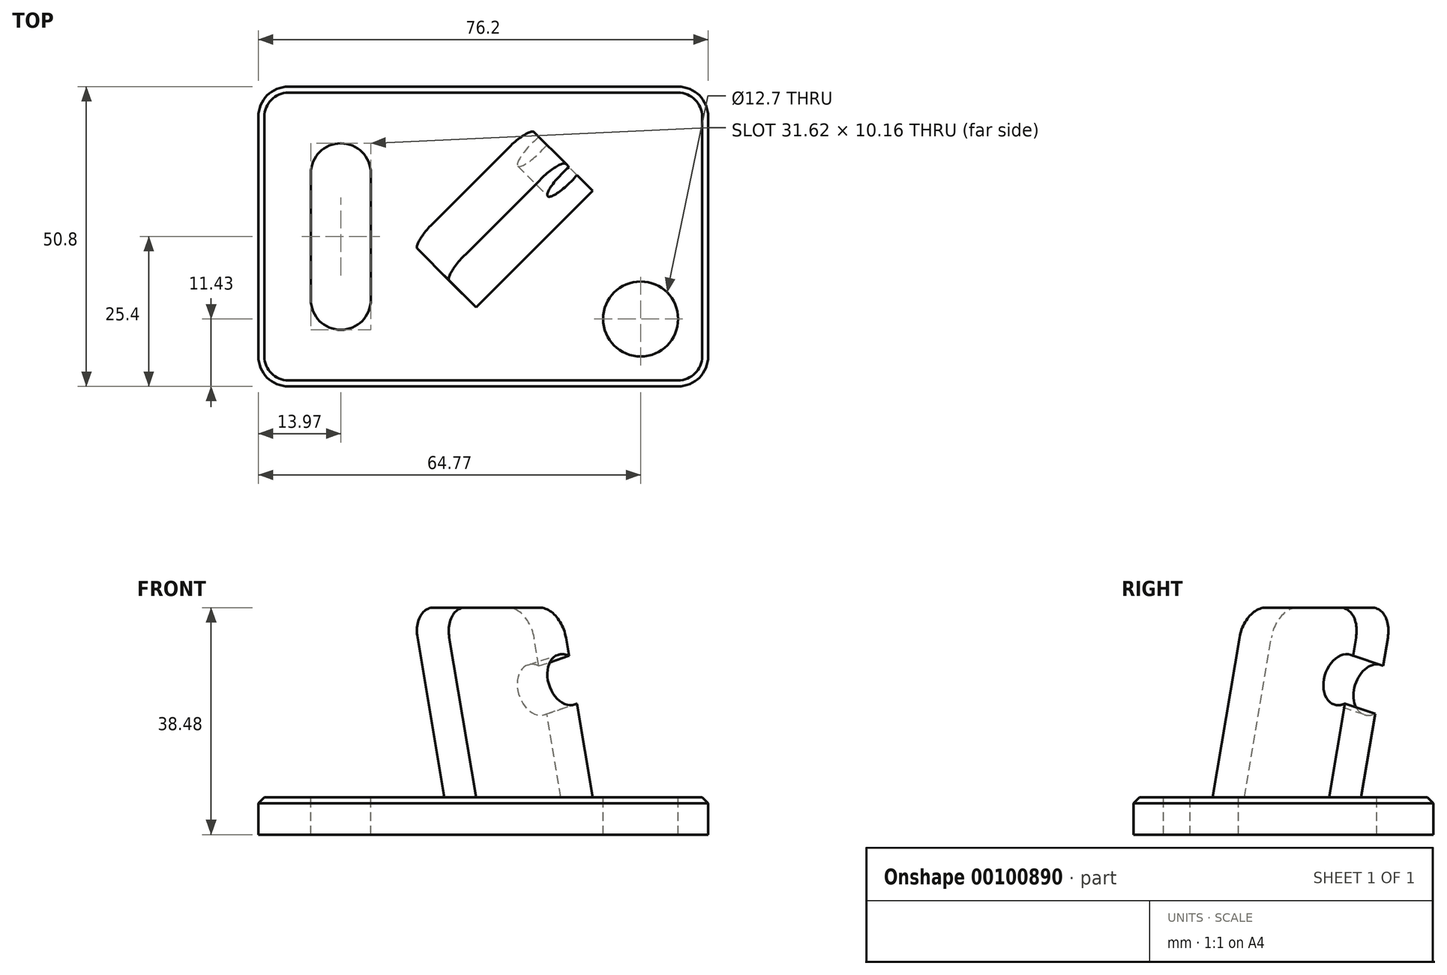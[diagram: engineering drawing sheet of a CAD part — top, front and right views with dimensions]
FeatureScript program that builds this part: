
annotation { "Feature Type Name" : "Feature", "Feature Type Description" : "" }
export const myFeature = defineFeature(function(context is Context, id is Id, definition is map)
    precondition{}
    {
        {
            var Q0;
            Q0=qCreatedBy(makeId("Top.planeOp"),FACE);
            var sketch = newSketch(context, id + "F0", { "sketchPlane" : qUnion([Q0])});
            skLineSegment(sketch, "E0", {"start": v(0, 25.4) * mm, "end": v(38.1, 25.4) * mm});
            skLineSegment(sketch, "E1", {"start": v(38.1, 25.4) * mm, "end": v(38.1, 0) * mm});
            skLineSegment(sketch, "E2.MirrorCS", {"start": v(0, 25.4) * mm, "end": v(-38.1, 25.4) * mm});
            skLineSegment(sketch, "E3.MirrorCS", {"start": v(-38.1, 25.4) * mm, "end": v(-38.1, 0) * mm});
            skLineSegment(sketch, "E4.MirrorCS", {"start": v(-38.1, -25.4) * mm, "end": v(-38.1, 0) * mm});
            skLineSegment(sketch, "E5.MirrorCS", {"start": v(0, -25.4) * mm, "end": v(-38.1, -25.4) * mm});
            skLineSegment(sketch, "E6.MirrorCS", {"start": v(0, -25.4) * mm, "end": v(38.1, -25.4) * mm});
            skLineSegment(sketch, "E7.MirrorCS", {"start": v(38.1, -25.4) * mm, "end": v(38.1, 0) * mm});
            skSolve(sketch);
        }
        {
            var Q0;
            Q0 = qSketchRegion(id + "F0", true);
            extrude(context, id + "F1", {"entities" : qUnion([Q0]), "depth" : 6.35 * mm});
        }
        {
            var Q0;
            Q0=makeQuery(id+"F1.opExtrude","CAP_FACE",FACE,{"disambiguationData":[OSD([sQuery(id+"F0.wireOp",EDGE,"E0"),sQuery(id+"F0.wireOp",EDGE,"E1"),sQuery(id+"F0.wireOp",EDGE,"E2.MirrorCS"),sQuery(id+"F0.wireOp",EDGE,"E3.MirrorCS"),sQuery(id+"F0.wireOp",EDGE,"E4.MirrorCS"),sQuery(id+"F0.wireOp",EDGE,"E5.MirrorCS"),sQuery(id+"F0.wireOp",EDGE,"E6.MirrorCS"),sQuery(id+"F0.wireOp",EDGE,"E7.MirrorCS")])],"isStart":false});
            var sketch = newSketch(context, id + "F2", { "sketchPlane" : qUnion([Q0])});
            skCircle(sketch, "E8", {"center": v(26.67, -13.97) * mm, "radius": 6.35 * mm});
            skArc(sketch, "E9", {"start": v(-19.05, 10.73) * mm, "mid": v(-24.13, 15.8) * mm, "end": v(-29.21, 10.73) * mm});
            skLineSegment(sketch, "E10", {"start": v(-29.21, 10.73) * mm, "end": v(-29.21, 0) * mm});
            skLineSegment(sketch, "E11", {"start": v(-19.05, 10.73) * mm, "end": v(-19.05, 0) * mm});
            skLineSegment(sketch, "E12.MirrorCS", {"start": v(-19.05, -10.73) * mm, "end": v(-19.05, 0) * mm});
            skLineSegment(sketch, "E13.MirrorCS", {"start": v(-29.21, -10.73) * mm, "end": v(-29.21, 0) * mm});
            skArc(sketch, "E14.MirrorCS", {"start": v(-19.05, -10.73) * mm, "mid": v(-24.13, -15.8) * mm, "end": v(-29.21, -10.73) * mm});
            skSolve(sketch);
        }
        {
            var Q0;
            Q0=makeQuery(id+"F2.imprint","IMPRINT",FACE,{"disambiguationData":[TD([[makeQuery(id+"F2.imprint","IMPRINT",EDGE,{"derivedFrom":sQuery(id+"F2.wireOp",EDGE,"E9")}),1.0]])]});
            var Q1;
            Q1=makeQuery(id+"F2.imprint","IMPRINT",FACE,{"disambiguationData":[TD([[makeQuery(id+"F2.imprint","IMPRINT",EDGE,{"derivedFrom":sQuery(id+"F2.wireOp",EDGE,"E8")}),1.0]])]});
            extrude(context, id + "F3", {"entities" : qUnion([Q0, Q1]), "operationType" : NewBodyOperationType.REMOVE, "oppositeDirection" : true, "depth" : 25.4 * mm});
        }
        {
            var Q0;
            Q0=makeQuery(id+"F1.opExtrude","SWEPT_EDGE",EDGE,{"disambiguationData":[OSD([sQuery(id+"F0.wireOp",EDGE,"E4.MirrorCS"),sQuery(id+"F0.wireOp",EDGE,"E5.MirrorCS")])]});
            cPlane(context, id + "F4", {"entities" : qUnion([Q0]), "cplaneType" : CPlaneType.LINE_ANGLE, "offset" : 152.4 * mm, "angle" : 135 * degree, "width" : 152.4 * mm, "height" : 152.4 * mm});
        }
        {
            var Q0;
            Q0=qCreatedBy(id+"F4.planeOp",FACE);
            var sketch = newSketch(context, id + "F5", { "sketchPlane" : qUnion([Q0])});
            skLineSegment(sketch, "E15", {"start": v(0, 6.35) * mm, "end": v(-7.62, 6.35) * mm});
            skLineSegment(sketch, "E16", {"start": v(0, 6.35) * mm, "end": v(7.62, 38.48) * mm});
            skLineSegment(sketch, "E17", {"start": v(0, 38.48) * mm, "end": v(7.62, 38.48) * mm});
            skLineSegment(sketch, "E18", {"start": v(0, 38.48) * mm, "end": v(-7.62, 6.35) * mm});
            skSolve(sketch);
        }
        {
            var Q0;
            Q0 = qSketchRegion(id + "F5", true);
            extrude(context, id + "F6", {"entities" : qUnion([Q0]), "operationType" : NewBodyOperationType.ADD, "depth" : 63.5 * mm, "hasSecondDirection" : true, "secondDirectionOppositeDirection" : false, "secondDirectionDepth" : 35.56 * mm});
        }
        {
            var Q0;
            Q0=makeQuery(id+"F6.opExtrude","CAP_EDGE",EDGE,{"disambiguationData":[OSD([sQuery(id+"F5.wireOp",EDGE,"E17")])],"isStart":true});
            var Q1;
            Q1=makeQuery(id+"F6.opExtrude","CAP_EDGE",EDGE,{"disambiguationData":[OSD([sQuery(id+"F5.wireOp",EDGE,"E17")])],"isStart":false});
            fillet(context, id + "F7", {"entities" : qUnion([Q0, Q1]), "radius" : 5.08 * mm, "tangentPropagation" : true, "allowEdgeOverflow" : false});
        }
        {
            var Q0;
            Q0=makeQuery(id+"F6.opExtrude","SWEPT_FACE",FACE,{"disambiguationData":[OSD([sQuery(id+"F5.wireOp",EDGE,"E18")])]});
            var sketch = newSketch(context, id + "F8", { "sketchPlane" : qUnion([Q0])});
            skCircle(sketch, "E19", {"center": v(10.99, 28.07) * mm, "radius": 4.45 * mm});
            skSolve(sketch);
        }
        {
            var Q0;
            Q0 = qSketchRegion(id + "F8", true);
            extrude(context, id + "F9", {"entities" : qUnion([Q0]), "operationType" : NewBodyOperationType.REMOVE, "oppositeDirection" : true, "depth" : 25.4 * mm});
        }
        {
            var Q0;
            Q0=makeQuery(id+"F1.opExtrude","SWEPT_EDGE",EDGE,{"disambiguationData":[OSD([sQuery(id+"F0.wireOp",EDGE,"E6.MirrorCS"),sQuery(id+"F0.wireOp",EDGE,"E7.MirrorCS")])]});
            var Q1;
            Q1=makeQuery(id+"F1.opExtrude","SWEPT_EDGE",EDGE,{"disambiguationData":[OSD([sQuery(id+"F0.wireOp",EDGE,"E0"),sQuery(id+"F0.wireOp",EDGE,"E1")])]});
            var Q2;
            Q2=makeQuery(id+"F1.opExtrude","SWEPT_EDGE",EDGE,{"disambiguationData":[OSD([sQuery(id+"F0.wireOp",EDGE,"E4.MirrorCS"),sQuery(id+"F0.wireOp",EDGE,"E5.MirrorCS")])]});
            var Q3;
            Q3=makeQuery(id+"F1.opExtrude","SWEPT_EDGE",EDGE,{"disambiguationData":[OSD([sQuery(id+"F0.wireOp",EDGE,"E2.MirrorCS"),sQuery(id+"F0.wireOp",EDGE,"E3.MirrorCS")])]});
            fillet(context, id + "F10", {"entities" : qUnion([Q0, Q1, Q2, Q3]), "radius" : 5.08 * mm, "tangentPropagation" : true, "allowEdgeOverflow" : false});
        }
        {
            var Q0;
            Q0=makeQuery(id+"F1.opExtrude","CAP_EDGE",EDGE,{"disambiguationData":[OSD([sQuery(id+"F0.wireOp",EDGE,"E5.MirrorCS"),sQuery(id+"F0.wireOp",EDGE,"E6.MirrorCS")])],"isStart":false});
            var Q1;
            Q1=makeQuery(id+"F1.opExtrude","CAP_EDGE",EDGE,{"disambiguationData":[OSD([sQuery(id+"F0.wireOp",EDGE,"E1"),sQuery(id+"F0.wireOp",EDGE,"E7.MirrorCS")])],"isStart":false});
            var Q2;
            {var subQ0=sQuery(id+"F0.wireOp",EDGE,"E7.MirrorCS");var subQ1=sQuery(id+"F0.wireOp",EDGE,"E6.MirrorCS");Q2=makeQuery(id+"F10.opFillet","BLEND_EDGE",EDGE,{"blendedFrom":[makeQuery(id+"F1.opExtrude","SWEPT_EDGE",EDGE,{"disambiguationData":[OSD([subQ1,subQ0])]}),makeQuery(id+"F1.opExtrude","CAP_FACE",FACE,{"disambiguationData":[OSD([sQuery(id+"F0.wireOp",EDGE,"E0"),sQuery(id+"F0.wireOp",EDGE,"E1"),sQuery(id+"F0.wireOp",EDGE,"E2.MirrorCS"),sQuery(id+"F0.wireOp",EDGE,"E3.MirrorCS"),sQuery(id+"F0.wireOp",EDGE,"E4.MirrorCS"),sQuery(id+"F0.wireOp",EDGE,"E5.MirrorCS"),subQ1,subQ0])],"isStart":false})],"blendedInto":[makeQuery(id+"F1.opExtrude","CAP_FACE",FACE,{"disambiguationData":[OSD([sQuery(id+"F0.wireOp",EDGE,"E0"),sQuery(id+"F0.wireOp",EDGE,"E1"),sQuery(id+"F0.wireOp",EDGE,"E2.MirrorCS"),sQuery(id+"F0.wireOp",EDGE,"E3.MirrorCS"),sQuery(id+"F0.wireOp",EDGE,"E4.MirrorCS"),sQuery(id+"F0.wireOp",EDGE,"E5.MirrorCS"),subQ1,subQ0])],"isStart":false})]});}
            var Q3;
            {var subQ0=sQuery(id+"F0.wireOp",EDGE,"E1");var subQ1=sQuery(id+"F0.wireOp",EDGE,"E0");Q3=makeQuery(id+"F10.opFillet","BLEND_EDGE",EDGE,{"blendedFrom":[makeQuery(id+"F1.opExtrude","SWEPT_EDGE",EDGE,{"disambiguationData":[OSD([subQ1,subQ0])]}),makeQuery(id+"F1.opExtrude","CAP_FACE",FACE,{"disambiguationData":[OSD([subQ1,subQ0,sQuery(id+"F0.wireOp",EDGE,"E2.MirrorCS"),sQuery(id+"F0.wireOp",EDGE,"E3.MirrorCS"),sQuery(id+"F0.wireOp",EDGE,"E4.MirrorCS"),sQuery(id+"F0.wireOp",EDGE,"E5.MirrorCS"),sQuery(id+"F0.wireOp",EDGE,"E6.MirrorCS"),sQuery(id+"F0.wireOp",EDGE,"E7.MirrorCS")])],"isStart":false})],"blendedInto":[makeQuery(id+"F1.opExtrude","CAP_FACE",FACE,{"disambiguationData":[OSD([subQ1,subQ0,sQuery(id+"F0.wireOp",EDGE,"E2.MirrorCS"),sQuery(id+"F0.wireOp",EDGE,"E3.MirrorCS"),sQuery(id+"F0.wireOp",EDGE,"E4.MirrorCS"),sQuery(id+"F0.wireOp",EDGE,"E5.MirrorCS"),sQuery(id+"F0.wireOp",EDGE,"E6.MirrorCS"),sQuery(id+"F0.wireOp",EDGE,"E7.MirrorCS")])],"isStart":false})]});}
            var Q4;
            Q4=makeQuery(id+"F1.opExtrude","CAP_EDGE",EDGE,{"disambiguationData":[OSD([sQuery(id+"F0.wireOp",EDGE,"E0"),sQuery(id+"F0.wireOp",EDGE,"E2.MirrorCS")])],"isStart":false});
            var Q5;
            {var subQ0=sQuery(id+"F0.wireOp",EDGE,"E3.MirrorCS");var subQ1=sQuery(id+"F0.wireOp",EDGE,"E2.MirrorCS");Q5=makeQuery(id+"F10.opFillet","BLEND_EDGE",EDGE,{"blendedFrom":[makeQuery(id+"F1.opExtrude","SWEPT_EDGE",EDGE,{"disambiguationData":[OSD([subQ1,subQ0])]}),makeQuery(id+"F1.opExtrude","CAP_FACE",FACE,{"disambiguationData":[OSD([sQuery(id+"F0.wireOp",EDGE,"E0"),sQuery(id+"F0.wireOp",EDGE,"E1"),subQ1,subQ0,sQuery(id+"F0.wireOp",EDGE,"E4.MirrorCS"),sQuery(id+"F0.wireOp",EDGE,"E5.MirrorCS"),sQuery(id+"F0.wireOp",EDGE,"E6.MirrorCS"),sQuery(id+"F0.wireOp",EDGE,"E7.MirrorCS")])],"isStart":false})],"blendedInto":[makeQuery(id+"F1.opExtrude","CAP_FACE",FACE,{"disambiguationData":[OSD([sQuery(id+"F0.wireOp",EDGE,"E0"),sQuery(id+"F0.wireOp",EDGE,"E1"),subQ1,subQ0,sQuery(id+"F0.wireOp",EDGE,"E4.MirrorCS"),sQuery(id+"F0.wireOp",EDGE,"E5.MirrorCS"),sQuery(id+"F0.wireOp",EDGE,"E6.MirrorCS"),sQuery(id+"F0.wireOp",EDGE,"E7.MirrorCS")])],"isStart":false})]});}
            var Q6;
            Q6=makeQuery(id+"F1.opExtrude","CAP_EDGE",EDGE,{"disambiguationData":[OSD([sQuery(id+"F0.wireOp",EDGE,"E3.MirrorCS"),sQuery(id+"F0.wireOp",EDGE,"E4.MirrorCS")])],"isStart":false});
            var Q7;
            {var subQ0=sQuery(id+"F0.wireOp",EDGE,"E5.MirrorCS");var subQ1=sQuery(id+"F0.wireOp",EDGE,"E4.MirrorCS");Q7=makeQuery(id+"F10.opFillet","BLEND_EDGE",EDGE,{"blendedFrom":[makeQuery(id+"F1.opExtrude","SWEPT_EDGE",EDGE,{"disambiguationData":[OSD([subQ1,subQ0])]}),makeQuery(id+"F1.opExtrude","CAP_FACE",FACE,{"disambiguationData":[OSD([sQuery(id+"F0.wireOp",EDGE,"E0"),sQuery(id+"F0.wireOp",EDGE,"E1"),sQuery(id+"F0.wireOp",EDGE,"E2.MirrorCS"),sQuery(id+"F0.wireOp",EDGE,"E3.MirrorCS"),subQ1,subQ0,sQuery(id+"F0.wireOp",EDGE,"E6.MirrorCS"),sQuery(id+"F0.wireOp",EDGE,"E7.MirrorCS")])],"isStart":false})],"blendedInto":[makeQuery(id+"F1.opExtrude","CAP_FACE",FACE,{"disambiguationData":[OSD([sQuery(id+"F0.wireOp",EDGE,"E0"),sQuery(id+"F0.wireOp",EDGE,"E1"),sQuery(id+"F0.wireOp",EDGE,"E2.MirrorCS"),sQuery(id+"F0.wireOp",EDGE,"E3.MirrorCS"),subQ1,subQ0,sQuery(id+"F0.wireOp",EDGE,"E6.MirrorCS"),sQuery(id+"F0.wireOp",EDGE,"E7.MirrorCS")])],"isStart":false})]});}
            chamfer(context, id + "F11", {"entities" : qUnion([Q0, Q1, Q2, Q3, Q4, Q5, Q6, Q7]), "width" : 1.02 * mm, "tangentPropagation" : true});
        }
    });
